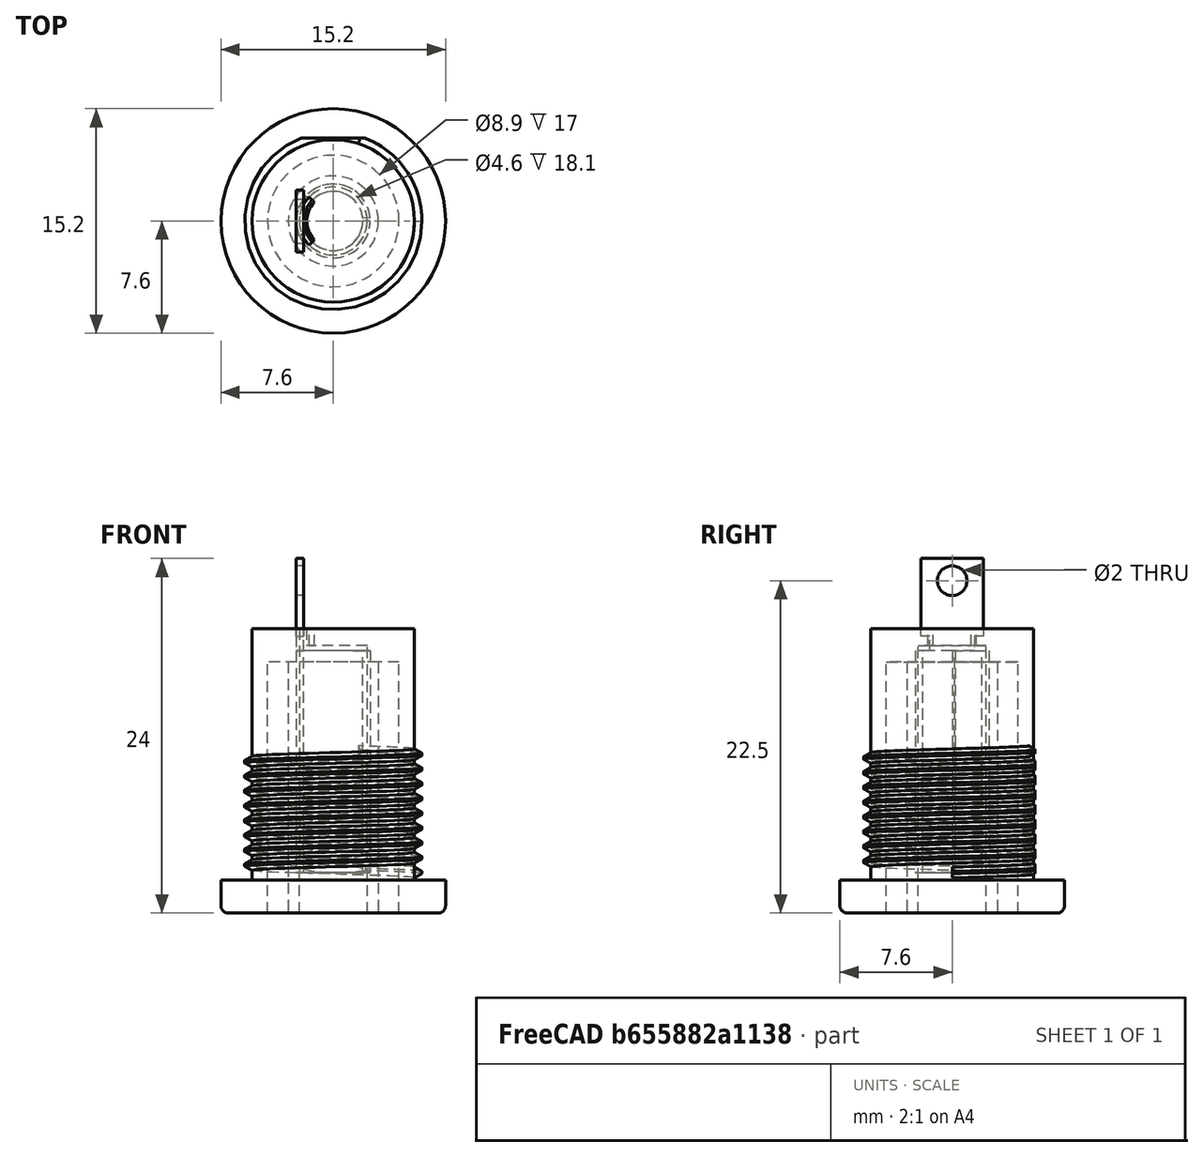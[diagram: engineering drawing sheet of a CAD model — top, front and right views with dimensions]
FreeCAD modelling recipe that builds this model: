
FCSTD DOCUMENT  (FreeCAD 0.15R4671 (Git))
Label: HBS_2D
License: All rights reserved
LicenseURL: http://en.wikipedia.org/wiki/All_rights_reserved
objects: App::FeaturePython×4, Drawing::FeatureViewPart×3, App::DocumentObjectGroup×2, Part::Feature×2, Drawing::FeatureViewPython×2, Part::Compound×1, Drawing::FeaturePage×1
note: 3 computed .brp shape members not serialized (recipe doc carries the construction recipe); baked Part::Feature solids carry a one-line shape summary decoded from their .brp

FEATURE [App::FeaturePython] Dimension  # Draft dimension (typed FeaturePython)
  Dimline = (11.8708,0,-0.669971)
  Direction = (0,0,0)
  Distance = 17
  End = (7.6,0,-0.5)
  Normal = (0,-1,0)
  Start = (7.6,0,16.5)
FEATURE [App::FeaturePython] Dimension001  # Draft dimension (typed FeaturePython)
  Dimline = (11.8696,0,-1.51157)
  Direction = (0,0,0)
  Distance = 2.25
  End = (7.6,0,-2.75)
  Normal = (0,-1,0)
  Start = (7.6,0,-0.5)
FEATURE [App::FeaturePython] Dimension002  # Draft dimension (typed FeaturePython)
  Dimline = (4.46714,1.30853e-06,21.9534)
  Direction = (0,0,0)
  Distance = 12.0065
  End = (6,-1.55762e-07,7.85564)
  Normal = (0,-1,5.9605e-08)
  Start = (-6.00647,-1.55762e-07,7.85564)
FEATURE [App::DocumentObjectGroup] Group  label="Cotas_z"
  Group = -> [Dimension,Dimension001,Dimension002]
FEATURE [Part::Feature] Cut001001  label="Cuerpo001"
  shape: bbox 17.88 x 17.56 x 19.25 mm, 71 faces (baked)
FEATURE [Part::Feature] Cut002001  label="Inserto"
  shape: bbox 5 x 5 x 21.25 mm, 19 faces (baked)
FEATURE [Part::Compound] Compound  label="Borne"
  Links = -> [Cut001001,Cut002001]
FEATURE [App::FeaturePython] Dimension003  # Draft dimension (typed FeaturePython)
  Dimline = (-3.66503,2.66715,0)
  Direction = (0,0,0)
  Distance = 4
  End = (-1.61712,1.17683,0)
  LinkedGeometry = -> [Cut002001]
  Normal = (0,0,-1)
  Start = (1.61712,-1.17683,0)
  Support = -> Cut002001
FEATURE [App::DocumentObjectGroup] Group001  label="Cota_inserto"
  Group = -> [Dimension003]
FEATURE [Drawing::FeatureViewPart] Ortho  label="Ortho_0_0"
  Direction = (0,0,1)
  HiddenWidth = 0.15
  LineWidth = 0.5
  Rotation = 0
  Scale = 2
  ShowHiddenLines = false
  ShowSmoothLines = false
  Source = -> Compound
  Tolerance = 0.05
  ViewResult = <blob: 6901 chars omitted>
  Visible = true
  X = 208.933
  Y = 50.3914
FEATURE [Drawing::FeatureViewPart] Ortho001  label="Ortho_0_-1"
  Direction = (0,-1,0)
  HiddenWidth = 0.15
  LineWidth = 0.5
  Rotation = 90
  Scale = 2
  ShowHiddenLines = false
  ShowSmoothLines = false
  Source = -> Compound
  Tolerance = 0.05
  ViewResult = <blob: 19564 chars omitted>
  Visible = true
  X = 208.933
  Y = 133.283
FEATURE [Drawing::FeatureViewPart] Ortho002  label="Ortho_-1_-1"
  Direction = (0.57735,-0.57735,-0.57735)
  HiddenWidth = 0.15
  LineWidth = 0.5
  Rotation = -60
  Scale = 2
  ShowHiddenLines = false
  ShowSmoothLines = false
  Source = -> Compound
  Tolerance = 0.05
  ViewResult = <blob: 11910 chars omitted>
  Visible = true
  X = 119.948
  Y = 107.23
FEATURE [Drawing::FeatureViewPython] ViewGroup  # drawing view (typed FeaturePython)
  Direction = (0,-1,0)
  FillStyle = 0
  FontSize = 12
  LineStyle = 0
  LineWidth = 0.35
  Rotation = 90
  Scale = 2
  Source = -> Group
  ViewResult = <blob: 3244 chars omitted>
  Visible = true
  X = 208.93
  Y = 133.28
FEATURE [Drawing::FeatureViewPython] ViewGroup001  # drawing view (typed FeaturePython)
  Direction = (0.58,-0.58,-0.58)
  FillStyle = 0
  FontSize = 12
  LineStyle = 0
  LineWidth = 0.35
  Rotation = -60
  Scale = 2
  Source = -> Group001
  ViewResult = <g id="ViewGroup001" transform="rotate(-60.0,119.95,107.23) translate(119.95,107.23) scale(2.0,-2.0)"><path d="M -1.14347707223 -0.30068793468 L -1.14347707223 -0.30068793468 L 1.14347707223 0.30068793468 L 1.14347707223 0.30068793468" fill="none" stroke="#0000ff" stroke-width="0.175 px" style="stroke-width:0.175;stroke-miterlimit:4;stroke-dasharray:none" freecad:basepoint1="-1.14347707223 -0.30068793468" freecad:basepoint2="1.14347707223 0.30068793468" freecad:dimpoint="-1.14347707223 -0.30068793468"/>\n<path transform="rotate(14.7329184638,-1.14347707223,-0.30068793468) translate(-1.14347707223,-0.30068793468) scale(0.666666666667,0.666666666667)" freecad:skip="1" fill="#0000ff" stroke="none" style="stroke-miterlimit:4;stroke-dasharray:none" d="M 0 0 L 4 1 L 4 -1 Z"/>\n<path transform="rotate(194.732918464,1.14347707223,0.30068793468) translate(1.14347707223,0.30068793468) scale(0.666666666667,0.666666666667)" freecad:skip="1" fill="#0000ff" stroke="none" style="stroke-miterlimit:4;stroke-dasharray:none" d="M 0 0 L 4 1 L 4 -1 Z"/>\n<text fill="#0000ff" font-size="3.0" style="text-anchor:middle;text-align:center;font-family:" transform="rotate(14.7329184638,-0.416070963081,0.900405478003) translate(-0.416070963081,0.900405478003) scale(1,-1) " freecad:skip="1">\nØ 4 </text>\n</g>
  Visible = true
  X = 119.95
  Y = 107.23
FEATURE [Drawing::FeaturePage] Page
  EditableTexts = Marcelo  | Marcelo | VioMar | type | HBS | 0001 | 05-02-2016
  Group = -> [Ortho,Ortho001,Ortho002,ViewGroup,ViewGroup001]
  Template = C:/Program Files/FreeCAD 0.15/data/Mod/Drawing/Templates/A4_Landscape_ISO7200.svg
